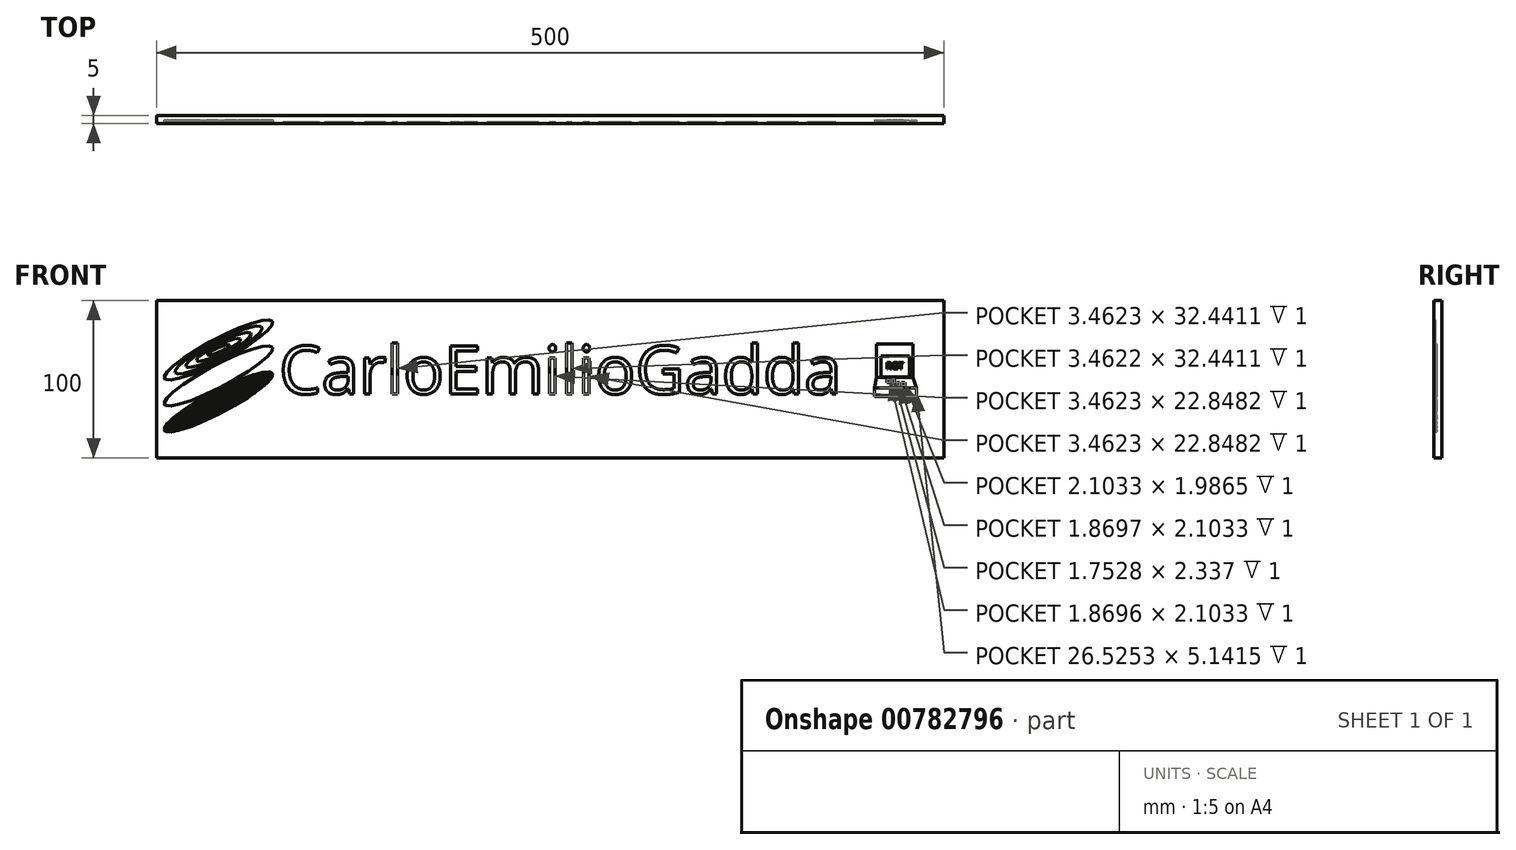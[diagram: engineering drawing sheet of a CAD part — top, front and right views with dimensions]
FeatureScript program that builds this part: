
annotation { "Feature Type Name" : "Feature", "Feature Type Description" : "" }
export const myFeature = defineFeature(function(context is Context, id is Id, definition is map)
    precondition{}
    {
        {
            var Q0;
            Q0=qCreatedBy(makeId("Front.planeOp"),FACE);
            var sketch = newSketch(context, id + "F0", { "sketchPlane" : qUnion([Q0])});
            skLineSegment(sketch, "E0.bottom", {"start": v(-240.28, 25.16) * mm, "end": v(259.72, 25.16) * mm});
            skLineSegment(sketch, "E0.top", {"start": v(-240.28, -74.84) * mm, "end": v(259.72, -74.84) * mm});
            skLineSegment(sketch, "E0.left", {"start": v(-240.28, 25.16) * mm, "end": v(-240.28, -74.84) * mm});
            skLineSegment(sketch, "E0.right", {"start": v(259.72, 25.16) * mm, "end": v(259.72, -74.84) * mm});
            skSolve(sketch);
        }
        {
            var Q0;
            Q0=makeQuery(id+"F0.imprint","IMPRINT",FACE,{"disambiguationData":[TD([[makeQuery(id+"F0.imprint","IMPRINT",EDGE,{"derivedFrom":sQuery(id+"F0.wireOp",EDGE,"E0.bottom")}),-1.0]])]});
            extrude(context, id + "F1", {"entities" : qUnion([Q0]), "depth" : 5 * mm, "offsetDistance" : 25 * mm});
        }
        {
            var Q0;
            Q0=makeQuery(id+"F1.opExtrude","CAP_FACE",FACE,{"disambiguationData":[OSD([sQuery(id+"F0.wireOp",EDGE,"E0.bottom"),sQuery(id+"F0.wireOp",EDGE,"E0.top"),sQuery(id+"F0.wireOp",EDGE,"E0.left"),sQuery(id+"F0.wireOp",EDGE,"E0.right")])],"isStart":false});
            var sketch = newSketch(context, id + "F2", { "sketchPlane" : qUnion([Q0])});
            skEllipse(sketch, "E1", {"center": v(-200.98, -6.22) * mm, "majorRadius": 38.81 * mm, "minorRadius": 7.02 * mm, "majorAxis": v(0.89, 0.47)});
            skEllipse(sketch, "E2.1.0.0", {"center": v(-200.98, -22.72) * mm, "majorRadius": 38.81 * mm, "minorRadius": 7.02 * mm, "majorAxis": v(0.89, 0.47)});
            skEllipse(sketch, "E2.2.0.0", {"center": v(-200.98, -39.22) * mm, "majorRadius": 38.81 * mm, "minorRadius": 7.02 * mm, "majorAxis": v(0.89, 0.47)});
            skLineSegment(sketch, "E2.direction1", {"start": v(-200.98, -6.22) * mm, "end": v(-200.98, -22.72) * mm, "construction": true});
            skText(sketch, "E3", { "text": "CarloEmilioGadda", "fontName": "OpenSans-Regular.ttf"});
            skLineSegment(sketch, "E4.bottom", {"start": v(219.86, -9.92) * mm, "end": v(237.74, -9.92) * mm});
            skLineSegment(sketch, "E4.top", {"start": v(219.86, -23.24) * mm, "end": v(237.74, -23.24) * mm});
            skLineSegment(sketch, "E4.left", {"start": v(219.86, -9.92) * mm, "end": v(219.86, -23.24) * mm});
            skLineSegment(sketch, "E4.right", {"start": v(237.74, -9.92) * mm, "end": v(237.74, -23.24) * mm});
            skLineSegment(sketch, "E5.bottom", {"start": v(215.65, -30.49) * mm, "end": v(242.18, -30.49) * mm});
            skLineSegment(sketch, "E5.top", {"start": v(215.65, -35.63) * mm, "end": v(242.18, -35.63) * mm});
            skLineSegment(sketch, "E5.left", {"start": v(215.65, -30.49) * mm, "end": v(215.65, -35.63) * mm});
            skLineSegment(sketch, "E5.right", {"start": v(242.18, -30.49) * mm, "end": v(242.18, -35.63) * mm});
            skLineSegment(sketch, "E6.bottom", {"start": v(229.8, -26.75) * mm, "end": v(231.66, -26.75) * mm});
            skLineSegment(sketch, "E6.top", {"start": v(229.8, -28.85) * mm, "end": v(231.66, -28.85) * mm});
            skLineSegment(sketch, "E6.left", {"start": v(229.8, -26.75) * mm, "end": v(229.8, -28.85) * mm});
            skLineSegment(sketch, "E6.right", {"start": v(231.66, -26.75) * mm, "end": v(231.66, -28.85) * mm});
            skLineSegment(sketch, "E7.bottom", {"start": v(232.83, -26.86) * mm, "end": v(234.93, -26.86) * mm});
            skLineSegment(sketch, "E7.top", {"start": v(232.83, -28.85) * mm, "end": v(234.93, -28.85) * mm});
            skLineSegment(sketch, "E7.left", {"start": v(232.83, -26.86) * mm, "end": v(232.83, -28.85) * mm});
            skLineSegment(sketch, "E7.right", {"start": v(234.93, -26.86) * mm, "end": v(234.93, -28.85) * mm});
            skLineSegment(sketch, "E8.bottom", {"start": v(223.71, -24.88) * mm, "end": v(225.58, -24.88) * mm});
            skLineSegment(sketch, "E8.top", {"start": v(223.71, -26.98) * mm, "end": v(225.58, -26.98) * mm});
            skLineSegment(sketch, "E8.left", {"start": v(223.71, -24.88) * mm, "end": v(223.71, -26.98) * mm});
            skLineSegment(sketch, "E8.right", {"start": v(225.58, -24.88) * mm, "end": v(225.58, -26.98) * mm});
            skLineSegment(sketch, "E9.bottom", {"start": v(226.64, -24.76) * mm, "end": v(228.39, -24.76) * mm});
            skLineSegment(sketch, "E9.top", {"start": v(226.64, -27.1) * mm, "end": v(228.39, -27.1) * mm});
            skLineSegment(sketch, "E9.left", {"start": v(226.64, -24.76) * mm, "end": v(226.64, -27.1) * mm});
            skLineSegment(sketch, "E9.right", {"start": v(228.39, -24.76) * mm, "end": v(228.39, -27.1) * mm});
            skLineSegment(sketch, "E10.bottom", {"start": v(216.91, -2.3) * mm, "end": v(239.95, -2.3) * mm});
            skLineSegment(sketch, "E10.top", {"start": v(216.91, -23.85) * mm, "end": v(239.95, -23.85) * mm});
            skLineSegment(sketch, "E10.left", {"start": v(216.91, -2.3) * mm, "end": v(216.91, -23.85) * mm});
            skLineSegment(sketch, "E10.right", {"start": v(239.95, -2.3) * mm, "end": v(239.95, -23.85) * mm});
            skLineSegment(sketch, "E11", {"start": v(216.91, -23.85) * mm, "end": v(215.65, -30.49) * mm});
            skLineSegment(sketch, "E12", {"start": v(239.95, -23.85) * mm, "end": v(242.18, -30.49) * mm});
            skText(sketch, "E13", { "text": "RGT", "fontName": "OpenSans-Regular.ttf"});
            skLineSegment(sketch, "E14", {"start": v(-235.33, -24.29) * mm, "end": v(-166.63, 11.85) * mm, "construction": true});
            skLineSegment(sketch, "E15", {"start": v(-204.25, 0) * mm, "end": v(-197.71, -12.43) * mm, "construction": true});
            skPoint(sketch, "E16", {"position": v(-235.33, -24.29) * mm});
            skPoint(sketch, "E17.1.0.0", {"position": v(-228.5, -20.5) * mm});
            skPoint(sketch, "E17.2.0.0", {"position": v(-221.68, -16.73) * mm});
            skPoint(sketch, "E17.3.0.0", {"position": v(-214.86, -12.95) * mm});
            skPoint(sketch, "E17.4.0.0", {"position": v(-208.03, -9.18) * mm});
            skLineSegment(sketch, "E17.direction1", {"start": v(-235.33, -24.29) * mm, "end": v(-228.5, -20.5) * mm, "construction": true});
            skPoint(sketch, "E18", {"position": v(-204.25, 0) * mm});
            skPoint(sketch, "E19.1.0.0", {"position": v(-203.57, -1.23) * mm});
            skPoint(sketch, "E19.2.0.0", {"position": v(-202.9, -2.46) * mm});
            skPoint(sketch, "E19.3.0.0", {"position": v(-202.22, -3.69) * mm});
            skPoint(sketch, "E19.4.0.0", {"position": v(-201.55, -4.91) * mm});
            skLineSegment(sketch, "E19.direction1", {"start": v(-204.25, 0) * mm, "end": v(-203.57, -1.23) * mm, "construction": true});
            skEllipse(sketch, "E20", {"center": v(-200.98, -6.22) * mm, "majorRadius": 31.01 * mm, "minorRadius": 5.62 * mm, "majorAxis": v(-0.89, -0.46)});
            skEllipse(sketch, "E21", {"center": v(-200.98, -6.22) * mm, "majorRadius": 23.22 * mm, "minorRadius": 4.22 * mm, "majorAxis": v(-0.9, -0.45)});
            skEllipse(sketch, "E22", {"center": v(-200.98, -6.22) * mm, "majorRadius": 15.42 * mm, "minorRadius": 2.82 * mm, "majorAxis": v(-0.9, -0.44)});
            skEllipse(sketch, "E23", {"center": v(-200.98, -6.22) * mm, "majorRadius": 7.65 * mm, "minorRadius": 1.43 * mm, "majorAxis": v(-0.92, -0.39)});
            skLineSegment(sketch, "E24", {"start": v(-235.33, -57.29) * mm, "end": v(-166.63, -21.15) * mm});
            skLineSegment(sketch, "E25.1.0.0", {"start": v(-234.84, -57.81) * mm, "end": v(-166.48, -21.85) * mm});
            skLineSegment(sketch, "E25.2.0.0", {"start": v(-234, -58.16) * mm, "end": v(-166.66, -22.74) * mm});
            skLineSegment(sketch, "E25.3.0.0", {"start": v(-232.81, -58.32) * mm, "end": v(-167.2, -23.8) * mm});
            skLineSegment(sketch, "E25.4.0.0", {"start": v(-231.23, -58.27) * mm, "end": v(-168.14, -25.08) * mm});
            skLineSegment(sketch, "E25.5.0.0", {"start": v(-229.22, -58) * mm, "end": v(-169.5, -26.59) * mm});
            skLineSegment(sketch, "E25.6.0.0", {"start": v(-226.69, -57.45) * mm, "end": v(-171.4, -28.36) * mm});
            skLineSegment(sketch, "E25.7.0.0", {"start": v(-223.5, -56.56) * mm, "end": v(-173.93, -30.48) * mm});
            skLineSegment(sketch, "E25.8.0.0", {"start": v(-219.4, -55.19) * mm, "end": v(-177.39, -33.09) * mm});
            skLineSegment(sketch, "E25.9.0.0", {"start": v(-213.72, -52.98) * mm, "end": v(-182.42, -36.52) * mm});
            skLineSegment(sketch, "E25.direction1", {"start": v(-235.33, -57.29) * mm, "end": v(-234.93, -57.86) * mm, "construction": true});
            skLineSegment(sketch, "E26.1.0.0", {"start": v(-235.48, -56.58) * mm, "end": v(-167.13, -20.62) * mm});
            skLineSegment(sketch, "E26.2.0.0", {"start": v(-235.3, -55.7) * mm, "end": v(-167.97, -20.28) * mm});
            skLineSegment(sketch, "E26.3.0.0", {"start": v(-234.74, -54.62) * mm, "end": v(-169.17, -20.12) * mm});
            skLineSegment(sketch, "E26.4.0.0", {"start": v(-233.8, -53.33) * mm, "end": v(-170.76, -20.17) * mm});
            skLineSegment(sketch, "E26.5.0.0", {"start": v(-232.41, -51.82) * mm, "end": v(-172.8, -20.45) * mm});
            skLineSegment(sketch, "E26.6.0.0", {"start": v(-230.5, -50.02) * mm, "end": v(-175.35, -21) * mm});
            skLineSegment(sketch, "E26.7.0.0", {"start": v(-227.94, -47.88) * mm, "end": v(-178.57, -21.91) * mm});
            skLineSegment(sketch, "E26.8.0.0", {"start": v(-224.43, -45.25) * mm, "end": v(-182.73, -23.31) * mm});
            skLineSegment(sketch, "E26.9.0.0", {"start": v(-219.3, -41.76) * mm, "end": v(-188.51, -25.57) * mm});
            skLineSegment(sketch, "E26.direction1", {"start": v(-235.33, -57.29) * mm, "end": v(-235.7, -56.7) * mm, "construction": true});
            skPoint(sketch, "E27.orphan", {"position": v(-238.72, -51.98) * mm});
            skPoint(sketch, "E28.orphan", {"position": v(-238.35, -52.57) * mm});
            skPoint(sketch, "E29.orphan", {"position": v(-237.97, -53.16) * mm});
            skPoint(sketch, "E30.orphan", {"position": v(-237.6, -53.75) * mm});
            skPoint(sketch, "E31.orphan", {"position": v(-236.84, -54.93) * mm});
            skPoint(sketch, "E32.orphan", {"position": v(-237.21, -54.34) * mm});
            skPoint(sketch, "E33.orphan", {"position": v(-236.46, -55.52) * mm});
            skPoint(sketch, "E34.orphan", {"position": v(-236.08, -56.1) * mm});
            skPoint(sketch, "E35.orphan", {"position": v(-234.52, -58.44) * mm});
            skPoint(sketch, "E36.orphan", {"position": v(-234.12, -59) * mm});
            skPoint(sketch, "E37.orphan", {"position": v(-233.72, -59.58) * mm});
            skPoint(sketch, "E38.orphan", {"position": v(-233.32, -60.16) * mm});
            skPoint(sketch, "E39.orphan", {"position": v(-232.92, -60.73) * mm});
            skPoint(sketch, "E40.orphan", {"position": v(-232.52, -61.3) * mm});
            skPoint(sketch, "E41.orphan", {"position": v(-232.12, -61.88) * mm});
            skPoint(sketch, "E42.orphan", {"position": v(-231.71, -62.45) * mm});
            skPoint(sketch, "E43.orphan", {"position": v(-163.02, -26.31) * mm});
            skPoint(sketch, "E44.orphan", {"position": v(-163.42, -25.74) * mm});
            skPoint(sketch, "E45.orphan", {"position": v(-163.82, -25.16) * mm});
            skPoint(sketch, "E46.orphan", {"position": v(-164.22, -24.6) * mm});
            skPoint(sketch, "E47.orphan", {"position": v(-164.62, -24.02) * mm});
            skPoint(sketch, "E48.orphan", {"position": v(-165.03, -23.44) * mm});
            skPoint(sketch, "E49.orphan", {"position": v(-165.43, -22.87) * mm});
            skPoint(sketch, "E50.orphan", {"position": v(-165.83, -22.3) * mm});
            skPoint(sketch, "E51.orphan", {"position": v(-166.23, -21.72) * mm});
            skPoint(sketch, "E52.orphan", {"position": v(-167, -20.56) * mm});
            skPoint(sketch, "E53.orphan", {"position": v(-167.39, -19.97) * mm});
            skPoint(sketch, "E54.orphan", {"position": v(-167.76, -19.38) * mm});
            skPoint(sketch, "E55.orphan", {"position": v(-168.14, -18.8) * mm});
            skPoint(sketch, "E56.orphan", {"position": v(-168.52, -18.2) * mm});
            skPoint(sketch, "E57.orphan", {"position": v(-168.9, -17.61) * mm});
            skPoint(sketch, "E58.orphan", {"position": v(-169.27, -17.02) * mm});
            skPoint(sketch, "E59.orphan", {"position": v(-170.03, -15.84) * mm});
            skPoint(sketch, "E60.orphan", {"position": v(-169.65, -16.43) * mm});
            const initialGuessF2  = {"E3": [-0.16247, -0.03418, 1, 0, 0.03074], "E13": [0.22292, -0.01836, 1, 0, 0.00424]};
            skSetInitialGuess(sketch, initialGuessF2);
            skSolve(sketch);
        }
        {
            var Q0;
            Q0=makeQuery(id+"F2.imprint","IMPRINT",FACE,{"disambiguationData":[TD([[makeQuery(id+"F2.imprint","IMPRINT",EDGE,{"derivedFrom":sQuery(id+"F2.wireOp",EDGE,"E2.1.0.0")}),1.0]])]});
            var Q1;
            Q1=makeQuery(id+"F2.imprint","IMPRINT",FACE,{"disambiguationData":[TD([[makeQuery(id+"F2.imprint","IMPRINT",EDGE,{"derivedFrom":sQuery(id+"F2.wireOp",EDGE,"E3.sketch_text.stroke-0")}),-1.0]])]});
            var Q2;
            Q2=makeQuery(id+"F2.imprint","IMPRINT",FACE,{"disambiguationData":[TD([[makeQuery(id+"F2.imprint","IMPRINT",EDGE,{"derivedFrom":sQuery(id+"F2.wireOp",EDGE,"E3.sketch_text.stroke-42")}),-1.0]])]});
            var Q3;
            Q3=makeQuery(id+"F2.imprint","IMPRINT",FACE,{"disambiguationData":[TD([[makeQuery(id+"F2.imprint","IMPRINT",EDGE,{"derivedFrom":sQuery(id+"F2.wireOp",EDGE,"E3.sketch_text.stroke-55")}),-1.0]])]});
            var Q4;
            Q4=makeQuery(id+"F2.imprint","IMPRINT",FACE,{"disambiguationData":[TD([[makeQuery(id+"F2.imprint","IMPRINT",EDGE,{"derivedFrom":sQuery(id+"F2.wireOp",EDGE,"E3.sketch_text.stroke-76")}),-1.0]])]});
            var Q5;
            Q5=makeQuery(id+"F2.imprint","IMPRINT",FACE,{"disambiguationData":[TD([[makeQuery(id+"F2.imprint","IMPRINT",EDGE,{"derivedFrom":sQuery(id+"F2.wireOp",EDGE,"E3.sketch_text.stroke-88")}),-1.0]])]});
            var Q6;
            Q6=makeQuery(id+"F2.imprint","IMPRINT",FACE,{"disambiguationData":[TD([[makeQuery(id+"F2.imprint","IMPRINT",EDGE,{"derivedFrom":sQuery(id+"F2.wireOp",EDGE,"E3.sketch_text.stroke-116")}),-1.0]])]});
            var Q7;
            Q7=makeQuery(id+"F2.imprint","IMPRINT",FACE,{"disambiguationData":[TD([[makeQuery(id+"F2.imprint","IMPRINT",EDGE,{"derivedFrom":sQuery(id+"F2.wireOp",EDGE,"E3.sketch_text.stroke-120")}),-1.0]])]});
            var Q8;
            Q8=makeQuery(id+"F2.imprint","IMPRINT",FACE,{"disambiguationData":[TD([[makeQuery(id+"F2.imprint","IMPRINT",EDGE,{"derivedFrom":sQuery(id+"F2.wireOp",EDGE,"E3.sketch_text.stroke-128")}),-1.0]])]});
            var Q9;
            Q9=makeQuery(id+"F2.imprint","IMPRINT",FACE,{"disambiguationData":[TD([[makeQuery(id+"F2.imprint","IMPRINT",EDGE,{"derivedFrom":sQuery(id+"F2.wireOp",EDGE,"E3.sketch_text.stroke-132")}),-1.0]])]});
            var Q10;
            Q10=makeQuery(id+"F2.imprint","IMPRINT",FACE,{"disambiguationData":[TD([[makeQuery(id+"F2.imprint","IMPRINT",EDGE,{"derivedFrom":sQuery(id+"F2.wireOp",EDGE,"E3.sketch_text.stroke-136")}),-1.0]])]});
            var Q11;
            Q11=makeQuery(id+"F2.imprint","IMPRINT",FACE,{"disambiguationData":[TD([[makeQuery(id+"F2.imprint","IMPRINT",EDGE,{"derivedFrom":sQuery(id+"F2.wireOp",EDGE,"E3.sketch_text.stroke-161")}),-1.0]])]});
            var Q12;
            Q12=makeQuery(id+"F2.imprint","IMPRINT",FACE,{"disambiguationData":[TD([[makeQuery(id+"F2.imprint","IMPRINT",EDGE,{"derivedFrom":sQuery(id+"F2.wireOp",EDGE,"E1")}),1.0]])]});
            var Q13;
            Q13=makeQuery(id+"F2.imprint","IMPRINT",FACE,{"disambiguationData":[TD([[makeQuery(id+"F2.imprint","IMPRINT",EDGE,{"derivedFrom":sQuery(id+"F2.wireOp",EDGE,"E3.sketch_text.stroke-15")}),-1.0]])]});
            var Q14;
            Q14=makeQuery(id+"F2.imprint","IMPRINT",FACE,{"disambiguationData":[TD([[makeQuery(id+"F2.imprint","IMPRINT",EDGE,{"derivedFrom":sQuery(id+"F2.wireOp",EDGE,"E3.sketch_text.stroke-59")}),-1.0]])]});
            var Q15;
            Q15=makeQuery(id+"F2.imprint","IMPRINT",FACE,{"disambiguationData":[TD([[makeQuery(id+"F2.imprint","IMPRINT",EDGE,{"derivedFrom":sQuery(id+"F2.wireOp",EDGE,"E3.sketch_text.stroke-144")}),-1.0]])]});
            var Q16;
            Q16=makeQuery(id+"F2.imprint","IMPRINT",FACE,{"disambiguationData":[TD([[makeQuery(id+"F2.imprint","IMPRINT",EDGE,{"derivedFrom":sQuery(id+"F2.wireOp",EDGE,"E3.sketch_text.stroke-181")}),-1.0]])]});
            var Q17;
            Q17=makeQuery(id+"F2.imprint","IMPRINT",FACE,{"disambiguationData":[TD([[makeQuery(id+"F2.imprint","IMPRINT",EDGE,{"derivedFrom":sQuery(id+"F2.wireOp",EDGE,"E3.sketch_text.stroke-208")}),-1.0]])]});
            var Q18;
            Q18=makeQuery(id+"F2.imprint","IMPRINT",FACE,{"disambiguationData":[TD([[makeQuery(id+"F2.imprint","IMPRINT",EDGE,{"derivedFrom":sQuery(id+"F2.wireOp",EDGE,"E3.sketch_text.stroke-232")}),-1.0]])]});
            var Q19;
            Q19=makeQuery(id+"F2.imprint","IMPRINT",FACE,{"disambiguationData":[TD([[makeQuery(id+"F2.imprint","IMPRINT",EDGE,{"derivedFrom":sQuery(id+"F2.wireOp",EDGE,"E3.sketch_text.stroke-256")}),-1.0]])]});
            var Q20;
            Q20=makeQuery(id+"F2.imprint","IMPRINT",FACE,{"disambiguationData":[TD([[makeQuery(id+"F2.imprint","IMPRINT",EDGE,{"derivedFrom":sQuery(id+"F2.wireOp",EDGE,"E5.bottom")}),-1.0]])]});
            var Q21;
            {var subQ0=sQuery(id+"F2.wireOp",EDGE,"dk1o7lyh-uNai-jobf-3xEU-I9IiX4PkBZ6V");Q21=makeQuery(id+"F2.imprint","IMPRINT",FACE,{"disambiguationData":[TD([[makeQuery(id+"F2.imprint","IMPRINT",EDGE,{"derivedFrom":subQ0}),1.0]])]});}
            var Q22;
            {var subQ0=sQuery(id+"F2.wireOp",EDGE,"d315a9da-9df5-4b53-9217-94c429a4e041.13.0");Q22=makeQuery(id+"F2.imprint","IMPRINT",FACE,{"disambiguationData":[TD([[makeQuery(id+"F2.imprint","IMPRINT",EDGE,{"derivedFrom":subQ0}),-1.0]])]});}
            var Q23;
            {var subQ0=sQuery(id+"F2.wireOp",EDGE,"d315a9da-9df5-4b53-9217-94c429a4e041.13.0");Q23=makeQuery(id+"F2.imprint","IMPRINT",FACE,{"disambiguationData":[TD([[makeQuery(id+"F2.imprint","IMPRINT",EDGE,{"derivedFrom":subQ0}),1.0]])]});}
            var Q24;
            {var subQ0=sQuery(id+"F2.wireOp",EDGE,"d315a9da-9df5-4b53-9217-94c429a4e041.14.0");Q24=makeQuery(id+"F2.imprint","IMPRINT",FACE,{"disambiguationData":[TD([[makeQuery(id+"F2.imprint","IMPRINT",EDGE,{"derivedFrom":subQ0}),1.0]])]});}
            var Q25;
            {var subQ0=sQuery(id+"F2.wireOp",EDGE,"6iQPFcGv-pmBH-5i8E-KgOV-sl3WbTSDHUFr");Q25=makeQuery(id+"F2.imprint","IMPRINT",FACE,{"disambiguationData":[TD([[makeQuery(id+"F2.imprint","IMPRINT",EDGE,{"derivedFrom":subQ0}),-1.0]])]});}
            var Q26;
            {var subQ0=sQuery(id+"F2.wireOp",EDGE,"6iQPFcGv-pmBH-5i8E-KgOV-sl3WbTSDHUFr");Q26=makeQuery(id+"F2.imprint","IMPRINT",FACE,{"disambiguationData":[TD([[makeQuery(id+"F2.imprint","IMPRINT",EDGE,{"derivedFrom":subQ0}),1.0]])]});}
            var Q27;
            {var subQ0=sQuery(id+"F2.wireOp",EDGE,"d315a9da-9df5-4b53-9217-94c429a4e041.1.0");Q27=makeQuery(id+"F2.imprint","IMPRINT",FACE,{"disambiguationData":[TD([[makeQuery(id+"F2.imprint","IMPRINT",EDGE,{"derivedFrom":subQ0}),1.0]])]});}
            var Q28;
            {var subQ0=sQuery(id+"F2.wireOp",EDGE,"d315a9da-9df5-4b53-9217-94c429a4e041.2.0");Q28=makeQuery(id+"F2.imprint","IMPRINT",FACE,{"disambiguationData":[TD([[makeQuery(id+"F2.imprint","IMPRINT",EDGE,{"derivedFrom":subQ0}),1.0]])]});}
            var Q29;
            {var subQ0=sQuery(id+"F2.wireOp",EDGE,"d315a9da-9df5-4b53-9217-94c429a4e041.5.0");Q29=makeQuery(id+"F2.imprint","IMPRINT",FACE,{"disambiguationData":[TD([[makeQuery(id+"F2.imprint","IMPRINT",EDGE,{"derivedFrom":subQ0}),-1.0]])]});}
            var Q30;
            {var subQ0=sQuery(id+"F2.wireOp",EDGE,"d315a9da-9df5-4b53-9217-94c429a4e041.5.0");Q30=makeQuery(id+"F2.imprint","IMPRINT",FACE,{"disambiguationData":[TD([[makeQuery(id+"F2.imprint","IMPRINT",EDGE,{"derivedFrom":subQ0}),1.0]])]});}
            var Q31;
            {var subQ0=sQuery(id+"F2.wireOp",EDGE,"d315a9da-9df5-4b53-9217-94c429a4e041.6.0");Q31=makeQuery(id+"F2.imprint","IMPRINT",FACE,{"disambiguationData":[TD([[makeQuery(id+"F2.imprint","IMPRINT",EDGE,{"derivedFrom":subQ0}),1.0]])]});}
            var Q32;
            {var subQ0=sQuery(id+"F2.wireOp",EDGE,"d315a9da-9df5-4b53-9217-94c429a4e041.7.0");Q32=makeQuery(id+"F2.imprint","IMPRINT",FACE,{"disambiguationData":[TD([[makeQuery(id+"F2.imprint","IMPRINT",EDGE,{"derivedFrom":subQ0}),1.0]])]});}
            var Q33;
            {var subQ0=sQuery(id+"F2.wireOp",EDGE,"d315a9da-9df5-4b53-9217-94c429a4e041.8.0");Q33=makeQuery(id+"F2.imprint","IMPRINT",FACE,{"disambiguationData":[TD([[makeQuery(id+"F2.imprint","IMPRINT",EDGE,{"derivedFrom":subQ0}),1.0]])]});}
            var Q34;
            {var subQ0=sQuery(id+"F2.wireOp",EDGE,"d315a9da-9df5-4b53-9217-94c429a4e041.9.0");Q34=makeQuery(id+"F2.imprint","IMPRINT",FACE,{"disambiguationData":[TD([[makeQuery(id+"F2.imprint","IMPRINT",EDGE,{"derivedFrom":subQ0}),1.0]])]});}
            var Q35;
            {var subQ0=sQuery(id+"F2.wireOp",EDGE,"d315a9da-9df5-4b53-9217-94c429a4e041.10.0");Q35=makeQuery(id+"F2.imprint","IMPRINT",FACE,{"disambiguationData":[TD([[makeQuery(id+"F2.imprint","IMPRINT",EDGE,{"derivedFrom":subQ0}),1.0]])]});}
            var Q36;
            {var subQ0=sQuery(id+"F2.wireOp",EDGE,"d315a9da-9df5-4b53-9217-94c429a4e041.11.0");Q36=makeQuery(id+"F2.imprint","IMPRINT",FACE,{"disambiguationData":[TD([[makeQuery(id+"F2.imprint","IMPRINT",EDGE,{"derivedFrom":subQ0}),1.0]])]});}
            var Q37;
            {var subQ0=sQuery(id+"F2.wireOp",EDGE,"dk1o7lyh-uNai-jobf-3xEU-I9IiX4PkBZ6V");Q37=makeQuery(id+"F2.imprint","IMPRINT",FACE,{"disambiguationData":[TD([[makeQuery(id+"F2.imprint","IMPRINT",EDGE,{"derivedFrom":subQ0}),-1.0]])]});}
            var Q38;
            Q38=makeQuery(id+"F2.imprint","IMPRINT",FACE,{"disambiguationData":[TD([[makeQuery(id+"F2.imprint","IMPRINT",EDGE,{"derivedFrom":sQuery(id+"F2.wireOp",EDGE,"E4.bottom")}),1.0]])]});
            var Q39;
            Q39=makeQuery(id+"F2.imprint","IMPRINT",FACE,{"disambiguationData":[TD([[makeQuery(id+"F2.imprint","IMPRINT",EDGE,{"derivedFrom":sQuery(id+"F2.wireOp",EDGE,"E5.bottom")}),1.0]])]});
            var Q40;
            Q40=makeQuery(id+"F2.imprint","IMPRINT",FACE,{"disambiguationData":[TD([[makeQuery(id+"F2.imprint","IMPRINT",EDGE,{"derivedFrom":sQuery(id+"F2.wireOp",EDGE,"E21")}),1.0]])]});
            var Q41;
            Q41=makeQuery(id+"F2.imprint","IMPRINT",FACE,{"disambiguationData":[TD([[makeQuery(id+"F2.imprint","IMPRINT",EDGE,{"derivedFrom":sQuery(id+"F2.wireOp",EDGE,"E23")}),1.0]])]});
            var Q42;
            {var subQ0=sQuery(id+"F2.wireOp",EDGE,"sn58d3Gb-LQ6R-2CsG-MgEA-buNP6vVM1N1h");Q42=makeQuery(id+"F2.imprint","IMPRINT",FACE,{"disambiguationData":[TD([[makeQuery(id+"F2.imprint","IMPRINT",EDGE,{"derivedFrom":subQ0}),1.0]])]});}
            var Q43;
            {var subQ0=sQuery(id+"F2.wireOp",EDGE,"sn58d3Gb-LQ6R-2CsG-MgEA-buNP6vVM1N1h");Q43=makeQuery(id+"F2.imprint","IMPRINT",FACE,{"disambiguationData":[TD([[makeQuery(id+"F2.imprint","IMPRINT",EDGE,{"derivedFrom":subQ0}),-1.0]])]});}
            var Q44;
            {var subQ0=sQuery(id+"F2.wireOp",EDGE,"d315a9da-9df5-4b53-9217-94c429a4e041.3.0");Q44=makeQuery(id+"F2.imprint","IMPRINT",FACE,{"disambiguationData":[TD([[makeQuery(id+"F2.imprint","IMPRINT",EDGE,{"derivedFrom":subQ0}),1.0]])]});}
            extrude(context, id + "F3", {"entities" : qUnion([Q0, Q1, Q2, Q3, Q4, Q5, Q6, Q7, Q8, Q9, Q10, Q11, Q12, Q13, Q14, Q15, Q16, Q17, Q18, Q19, Q20, Q21, Q22, Q23, Q24, Q25, Q26, Q27, Q28, Q29, Q30, Q31, Q32, Q33, Q34, Q35, Q36, Q37, Q38, Q39, Q40, Q41, Q42, Q43, Q44]), "operationType" : NewBodyOperationType.REMOVE, "oppositeDirection" : true, "depth" : 1 * mm, "offsetDistance" : 25 * mm});
        }
        {
            var Q0;
            Q0=makeQuery(id+"F2.imprint","IMPRINT",FACE,{"disambiguationData":[TD([[makeQuery(id+"F2.imprint","IMPRINT",EDGE,{"derivedFrom":sQuery(id+"F2.wireOp",EDGE,"E13.sketch_text.stroke-0")}),-1.0]])]});
            var Q1;
            Q1=makeQuery(id+"F2.imprint","IMPRINT",FACE,{"disambiguationData":[TD([[makeQuery(id+"F2.imprint","IMPRINT",EDGE,{"derivedFrom":sQuery(id+"F2.wireOp",EDGE,"E13.sketch_text.stroke-18")}),-1.0]])]});
            var Q2;
            Q2=makeQuery(id+"F2.imprint","IMPRINT",FACE,{"disambiguationData":[TD([[makeQuery(id+"F2.imprint","IMPRINT",EDGE,{"derivedFrom":sQuery(id+"F2.wireOp",EDGE,"E13.sketch_text.stroke-38")}),-1.0]])]});
            var Q3;
            {var subQ0=sQuery(id+"F2.wireOp",EDGE,"E26.9.0.0");Q3=makeQuery(id+"F2.imprint","IMPRINT",FACE,{"disambiguationData":[TD([[makeQuery(id+"F2.imprint","IMPRINT",EDGE,{"derivedFrom":subQ0}),1.0]])]});}
            var Q4;
            {var subQ0=sQuery(id+"F2.wireOp",EDGE,"E26.7.0.0");Q4=makeQuery(id+"F2.imprint","IMPRINT",FACE,{"disambiguationData":[TD([[makeQuery(id+"F2.imprint","IMPRINT",EDGE,{"derivedFrom":subQ0}),1.0]])]});}
            var Q5;
            {var subQ0=sQuery(id+"F2.wireOp",EDGE,"E26.5.0.0");Q5=makeQuery(id+"F2.imprint","IMPRINT",FACE,{"disambiguationData":[TD([[makeQuery(id+"F2.imprint","IMPRINT",EDGE,{"derivedFrom":subQ0}),1.0]])]});}
            var Q6;
            {var subQ0=sQuery(id+"F2.wireOp",EDGE,"E26.3.0.0");Q6=makeQuery(id+"F2.imprint","IMPRINT",FACE,{"disambiguationData":[TD([[makeQuery(id+"F2.imprint","IMPRINT",EDGE,{"derivedFrom":subQ0}),1.0]])]});}
            var Q7;
            {var subQ0=sQuery(id+"F2.wireOp",EDGE,"E26.1.0.0");Q7=makeQuery(id+"F2.imprint","IMPRINT",FACE,{"disambiguationData":[TD([[makeQuery(id+"F2.imprint","IMPRINT",EDGE,{"derivedFrom":subQ0}),1.0]])]});}
            var Q8;
            {var subQ0=sQuery(id+"F2.wireOp",EDGE,"E24");Q8=makeQuery(id+"F2.imprint","IMPRINT",FACE,{"disambiguationData":[TD([[makeQuery(id+"F2.imprint","IMPRINT",EDGE,{"derivedFrom":subQ0}),-1.0]])]});}
            var Q9;
            {var subQ0=sQuery(id+"F2.wireOp",EDGE,"E25.2.0.0");Q9=makeQuery(id+"F2.imprint","IMPRINT",FACE,{"disambiguationData":[TD([[makeQuery(id+"F2.imprint","IMPRINT",EDGE,{"derivedFrom":subQ0}),-1.0]])]});}
            var Q10;
            {var subQ0=sQuery(id+"F2.wireOp",EDGE,"E25.4.0.0");Q10=makeQuery(id+"F2.imprint","IMPRINT",FACE,{"disambiguationData":[TD([[makeQuery(id+"F2.imprint","IMPRINT",EDGE,{"derivedFrom":subQ0}),-1.0]])]});}
            var Q11;
            {var subQ0=sQuery(id+"F2.wireOp",EDGE,"E25.6.0.0");Q11=makeQuery(id+"F2.imprint","IMPRINT",FACE,{"disambiguationData":[TD([[makeQuery(id+"F2.imprint","IMPRINT",EDGE,{"derivedFrom":subQ0}),-1.0]])]});}
            var Q12;
            {var subQ0=sQuery(id+"F2.wireOp",EDGE,"E25.8.0.0");Q12=makeQuery(id+"F2.imprint","IMPRINT",FACE,{"disambiguationData":[TD([[makeQuery(id+"F2.imprint","IMPRINT",EDGE,{"derivedFrom":subQ0}),-1.0]])]});}
            var Q13;
            Q13=makeQuery(id+"F2.imprint","IMPRINT",FACE,{"disambiguationData":[TD([[makeQuery(id+"F2.imprint","IMPRINT",EDGE,{"derivedFrom":sQuery(id+"F2.wireOp",EDGE,"E8.bottom")}),-1.0]])]});
            var Q14;
            Q14=makeQuery(id+"F2.imprint","IMPRINT",FACE,{"disambiguationData":[TD([[makeQuery(id+"F2.imprint","IMPRINT",EDGE,{"derivedFrom":sQuery(id+"F2.wireOp",EDGE,"E9.bottom")}),-1.0]])]});
            var Q15;
            Q15=makeQuery(id+"F2.imprint","IMPRINT",FACE,{"disambiguationData":[TD([[makeQuery(id+"F2.imprint","IMPRINT",EDGE,{"derivedFrom":sQuery(id+"F2.wireOp",EDGE,"E6.bottom")}),-1.0]])]});
            var Q16;
            Q16=makeQuery(id+"F2.imprint","IMPRINT",FACE,{"disambiguationData":[TD([[makeQuery(id+"F2.imprint","IMPRINT",EDGE,{"derivedFrom":sQuery(id+"F2.wireOp",EDGE,"E7.bottom")}),-1.0]])]});
            extrude(context, id + "F4", {"entities" : qUnion([Q0, Q1, Q2, Q3, Q4, Q5, Q6, Q7, Q8, Q9, Q10, Q11, Q12, Q13, Q14, Q15, Q16]), "operationType" : NewBodyOperationType.REMOVE, "oppositeDirection" : true, "depth" : 1 * mm, "offsetDistance" : 25 * mm});
        }
        {
            var Q0;
            {var subQ0=sQuery(id+"F2.wireOp",EDGE,"E25.9.0.0");Q0=makeQuery(id+"F2.imprint","IMPRINT",FACE,{"disambiguationData":[TD([[makeQuery(id+"F2.imprint","IMPRINT",EDGE,{"derivedFrom":subQ0}),-1.0]])]});}
            var Q1;
            {var subQ0=sQuery(id+"F2.wireOp",EDGE,"E25.7.0.0");Q1=makeQuery(id+"F2.imprint","IMPRINT",FACE,{"disambiguationData":[TD([[makeQuery(id+"F2.imprint","IMPRINT",EDGE,{"derivedFrom":subQ0}),-1.0]])]});}
            var Q2;
            {var subQ0=sQuery(id+"F2.wireOp",EDGE,"E25.5.0.0");Q2=makeQuery(id+"F2.imprint","IMPRINT",FACE,{"disambiguationData":[TD([[makeQuery(id+"F2.imprint","IMPRINT",EDGE,{"derivedFrom":subQ0}),-1.0]])]});}
            var Q3;
            {var subQ0=sQuery(id+"F2.wireOp",EDGE,"E25.3.0.0");Q3=makeQuery(id+"F2.imprint","IMPRINT",FACE,{"disambiguationData":[TD([[makeQuery(id+"F2.imprint","IMPRINT",EDGE,{"derivedFrom":subQ0}),-1.0]])]});}
            var Q4;
            {var subQ0=sQuery(id+"F2.wireOp",EDGE,"E25.1.0.0");Q4=makeQuery(id+"F2.imprint","IMPRINT",FACE,{"disambiguationData":[TD([[makeQuery(id+"F2.imprint","IMPRINT",EDGE,{"derivedFrom":subQ0}),-1.0]])]});}
            var Q5;
            {var subQ0=sQuery(id+"F2.wireOp",EDGE,"E24");Q5=makeQuery(id+"F2.imprint","IMPRINT",FACE,{"disambiguationData":[TD([[makeQuery(id+"F2.imprint","IMPRINT",EDGE,{"derivedFrom":subQ0}),1.0]])]});}
            var Q6;
            {var subQ0=sQuery(id+"F2.wireOp",EDGE,"E26.2.0.0");Q6=makeQuery(id+"F2.imprint","IMPRINT",FACE,{"disambiguationData":[TD([[makeQuery(id+"F2.imprint","IMPRINT",EDGE,{"derivedFrom":subQ0}),1.0]])]});}
            var Q7;
            {var subQ0=sQuery(id+"F2.wireOp",EDGE,"E26.4.0.0");Q7=makeQuery(id+"F2.imprint","IMPRINT",FACE,{"disambiguationData":[TD([[makeQuery(id+"F2.imprint","IMPRINT",EDGE,{"derivedFrom":subQ0}),1.0]])]});}
            var Q8;
            {var subQ0=sQuery(id+"F2.wireOp",EDGE,"E26.6.0.0");Q8=makeQuery(id+"F2.imprint","IMPRINT",FACE,{"disambiguationData":[TD([[makeQuery(id+"F2.imprint","IMPRINT",EDGE,{"derivedFrom":subQ0}),1.0]])]});}
            var Q9;
            {var subQ0=sQuery(id+"F2.wireOp",EDGE,"E26.8.0.0");Q9=makeQuery(id+"F2.imprint","IMPRINT",FACE,{"disambiguationData":[TD([[makeQuery(id+"F2.imprint","IMPRINT",EDGE,{"derivedFrom":subQ0}),1.0]])]});}
            var Q10;
            Q10=makeQuery(id+"F2.imprint","IMPRINT",FACE,{"disambiguationData":[TD([[makeQuery(id+"F2.imprint","IMPRINT",EDGE,{"derivedFrom":sQuery(id+"F2.wireOp",EDGE,"E2.1.0.0")}),1.0]])]});
            var Q11;
            Q11=makeQuery(id+"F2.imprint","IMPRINT",FACE,{"disambiguationData":[TD([[makeQuery(id+"F2.imprint","IMPRINT",EDGE,{"derivedFrom":sQuery(id+"F2.wireOp",EDGE,"E13.sketch_text.stroke-0")}),-1.0]])]});
            var Q12;
            Q12=makeQuery(id+"F2.imprint","IMPRINT",FACE,{"disambiguationData":[TD([[makeQuery(id+"F2.imprint","IMPRINT",EDGE,{"derivedFrom":sQuery(id+"F2.wireOp",EDGE,"E13.sketch_text.stroke-18")}),-1.0]])]});
            var Q13;
            Q13=makeQuery(id+"F2.imprint","IMPRINT",FACE,{"disambiguationData":[TD([[makeQuery(id+"F2.imprint","IMPRINT",EDGE,{"derivedFrom":sQuery(id+"F2.wireOp",EDGE,"E13.sketch_text.stroke-38")}),-1.0]])]});
            var Q14;
            Q14=makeQuery(id+"F2.imprint","IMPRINT",FACE,{"disambiguationData":[TD([[makeQuery(id+"F2.imprint","IMPRINT",EDGE,{"derivedFrom":sQuery(id+"F2.wireOp",EDGE,"E4.bottom")}),1.0]])]});
            var Q15;
            Q15=makeQuery(id+"F2.imprint","IMPRINT",FACE,{"disambiguationData":[TD([[makeQuery(id+"F2.imprint","IMPRINT",EDGE,{"derivedFrom":sQuery(id+"F2.wireOp",EDGE,"E5.bottom")}),-1.0]])]});
            var Q16;
            Q16=makeQuery(id+"F2.imprint","IMPRINT",FACE,{"disambiguationData":[TD([[makeQuery(id+"F2.imprint","IMPRINT",EDGE,{"derivedFrom":sQuery(id+"F2.wireOp",EDGE,"E8.bottom")}),-1.0]])]});
            var Q17;
            Q17=makeQuery(id+"F2.imprint","IMPRINT",FACE,{"disambiguationData":[TD([[makeQuery(id+"F2.imprint","IMPRINT",EDGE,{"derivedFrom":sQuery(id+"F2.wireOp",EDGE,"E9.bottom")}),-1.0]])]});
            var Q18;
            Q18=makeQuery(id+"F2.imprint","IMPRINT",FACE,{"disambiguationData":[TD([[makeQuery(id+"F2.imprint","IMPRINT",EDGE,{"derivedFrom":sQuery(id+"F2.wireOp",EDGE,"E6.bottom")}),-1.0]])]});
            var Q19;
            Q19=makeQuery(id+"F2.imprint","IMPRINT",FACE,{"disambiguationData":[TD([[makeQuery(id+"F2.imprint","IMPRINT",EDGE,{"derivedFrom":sQuery(id+"F2.wireOp",EDGE,"E7.bottom")}),-1.0]])]});
            extrude(context, id + "F5", {"entities" : qUnion([Q0, Q1, Q2, Q3, Q4, Q5, Q6, Q7, Q8, Q9, Q10, Q11, Q12, Q13, Q14, Q15, Q16, Q17, Q18, Q19]), "operationType" : NewBodyOperationType.REMOVE, "oppositeDirection" : true, "depth" : 2 * mm, "offsetDistance" : 25 * mm});
        }
    });
